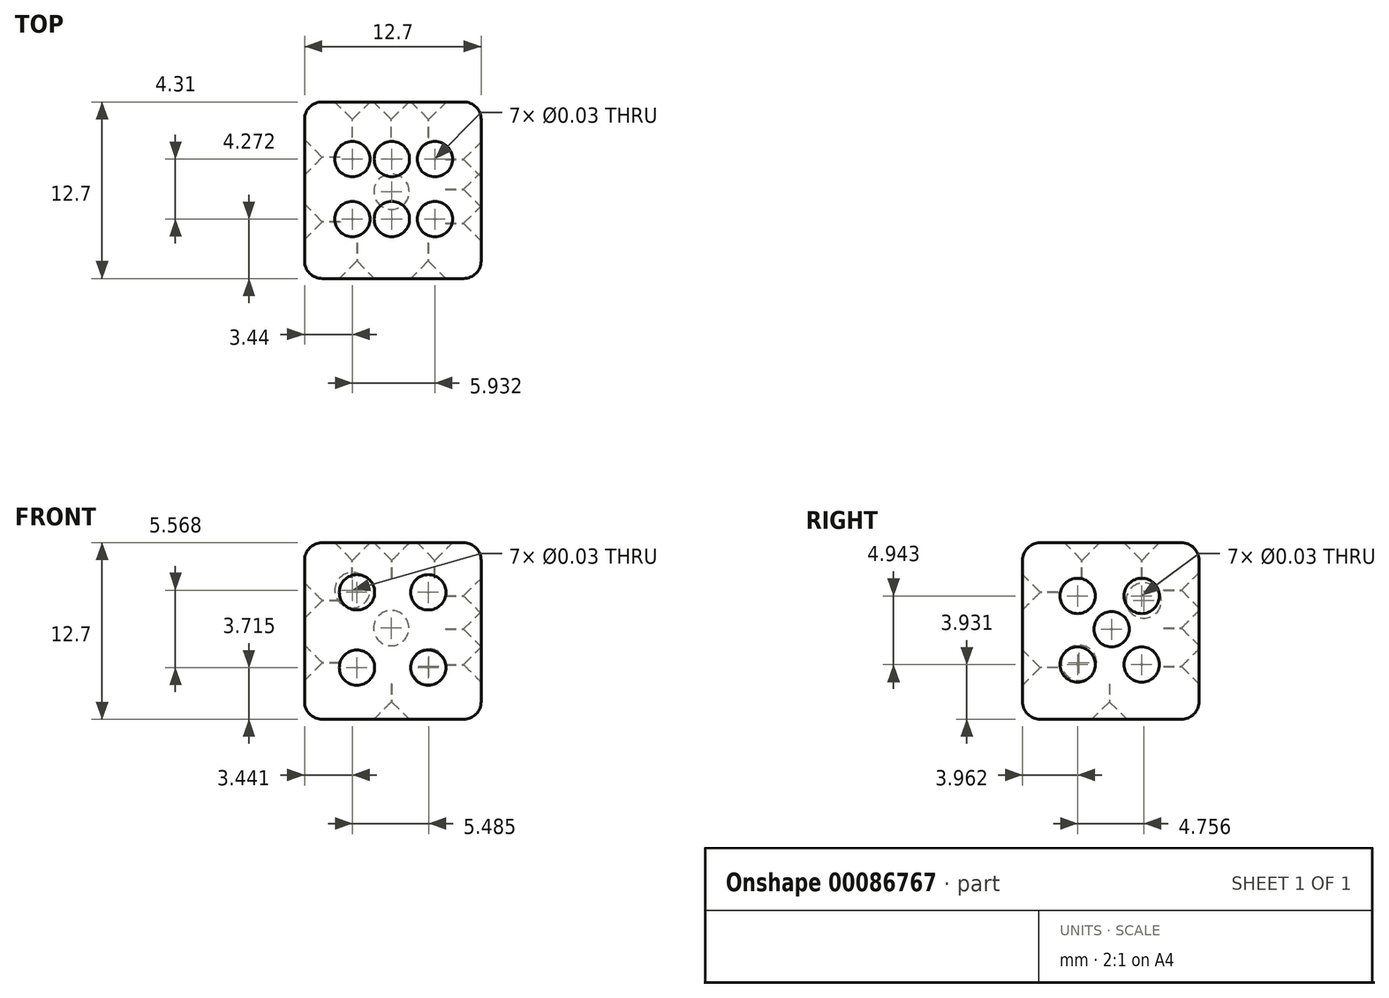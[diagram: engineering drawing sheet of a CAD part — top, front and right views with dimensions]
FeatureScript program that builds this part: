
annotation { "Feature Type Name" : "Feature", "Feature Type Description" : "" }
export const myFeature = defineFeature(function(context is Context, id is Id, definition is map)
    precondition{}
    {
        {
            var Q0;
            Q0=qCreatedBy(makeId("Front.planeOp"),FACE);
            var sketch = newSketch(context, id + "F0", { "sketchPlane" : qUnion([Q0])});
            skLineSegment(sketch, "E0.bottom", {"start": v(-48.45, 33.38) * mm, "end": v(-35.75, 33.38) * mm});
            skLineSegment(sketch, "E0.top", {"start": v(-48.45, 20.68) * mm, "end": v(-35.75, 20.68) * mm});
            skLineSegment(sketch, "E0.left", {"start": v(-48.45, 33.38) * mm, "end": v(-48.45, 20.68) * mm});
            skLineSegment(sketch, "E0.right", {"start": v(-35.75, 33.38) * mm, "end": v(-35.75, 20.68) * mm});
            skSolve(sketch);
        }
        {
            var Q0;
            Q0=makeQuery(id+"F0.imprint","IMPRINT",FACE,{"disambiguationData":[TD([[makeQuery(id+"F0.imprint","IMPRINT",EDGE,{"derivedFrom":sQuery(id+"F0.wireOp",EDGE,"E0.bottom")}),-1.0]])]});
            extrude(context, id + "F1", {"entities" : qUnion([Q0]), "depth" : 12.7 * mm});
        }
        {
            var Q0;
            Q0=makeQuery(id+"F1.opExtrude","SWEPT_EDGE",EDGE,{"disambiguationData":[OSD([sQuery(id+"F0.wireOp",EDGE,"E0.bottom"),sQuery(id+"F0.wireOp",EDGE,"E0.left")])]});
            var Q1;
            Q1=makeQuery(id+"F1.opExtrude","CAP_EDGE",EDGE,{"disambiguationData":[OSD([sQuery(id+"F0.wireOp",EDGE,"E0.bottom")])],"isStart":false});
            var Q2;
            Q2=makeQuery(id+"F1.opExtrude","SWEPT_EDGE",EDGE,{"disambiguationData":[OSD([sQuery(id+"F0.wireOp",EDGE,"E0.bottom"),sQuery(id+"F0.wireOp",EDGE,"E0.right")])]});
            var Q3;
            Q3=makeQuery(id+"F1.opExtrude","CAP_EDGE",EDGE,{"disambiguationData":[OSD([sQuery(id+"F0.wireOp",EDGE,"E0.right")])],"isStart":false});
            var Q4;
            Q4=makeQuery(id+"F1.opExtrude","CAP_EDGE",EDGE,{"disambiguationData":[OSD([sQuery(id+"F0.wireOp",EDGE,"E0.left")])],"isStart":false});
            var Q5;
            Q5=makeQuery(id+"F1.opExtrude","CAP_EDGE",EDGE,{"disambiguationData":[OSD([sQuery(id+"F0.wireOp",EDGE,"E0.bottom")])],"isStart":true});
            var Q6;
            Q6=makeQuery(id+"F1.opExtrude","CAP_EDGE",EDGE,{"disambiguationData":[OSD([sQuery(id+"F0.wireOp",EDGE,"E0.top")])],"isStart":false});
            var Q7;
            Q7=makeQuery(id+"F1.opExtrude","CAP_FACE",FACE,{"disambiguationData":[OSD([sQuery(id+"F0.wireOp",EDGE,"E0.bottom"),sQuery(id+"F0.wireOp",EDGE,"E0.top"),sQuery(id+"F0.wireOp",EDGE,"E0.left"),sQuery(id+"F0.wireOp",EDGE,"E0.right")])],"isStart":true});
            var Q8;
            Q8=makeQuery(id+"F1.opExtrude","SWEPT_FACE",FACE,{"disambiguationData":[OSD([sQuery(id+"F0.wireOp",EDGE,"E0.top")])]});
            fillet(context, id + "F2", {"entities" : qUnion([Q0, Q1, Q2, Q3, Q4, Q5, Q6, Q7, Q8]), "radius" : 1.27 * mm, "tangentPropagation" : true, "allowEdgeOverflow" : false});
        }
        {
            var Q0;
            Q0=makeQuery(id+"F1.opExtrude","SWEPT_FACE",FACE,{"disambiguationData":[OSD([sQuery(id+"F0.wireOp",EDGE,"E0.right")])]});
            var sketch = newSketch(context, id + "F3", { "sketchPlane" : qUnion([Q0])});
            skPoint(sketch, "E1", {"position": v(-8.74, 29.55) * mm});
            skPoint(sketch, "E2", {"position": v(-4.13, 29.55) * mm});
            skPoint(sketch, "E3", {"position": v(-4.13, 24.61) * mm});
            skPoint(sketch, "E4", {"position": v(-8.74, 24.61) * mm});
            skPoint(sketch, "E5", {"position": v(-6.3, 27.17) * mm});
            skSolve(sketch);
        }
        {
            var Q0;
            Q0=sQuery(id+"F3.wireOp",VERTEX,"E1");
            var Q1;
            Q1=sQuery(id+"F3.wireOp",VERTEX,"E2");
            var Q2;
            Q2=sQuery(id+"F3.wireOp",VERTEX,"E5");
            var Q3;
            Q3=sQuery(id+"F3.wireOp",VERTEX,"E3");
            var Q4;
            Q4=sQuery(id+"F3.wireOp",VERTEX,"E4");
            var Q5;
            Q5=makeQuery(id+"F1.opExtrude","SWEPT_BODY",BODY,{"disambiguationData":[OSD([sQuery(id+"F0.wireOp",EDGE,"E0.bottom"),sQuery(id+"F0.wireOp",EDGE,"E0.top"),sQuery(id+"F0.wireOp",EDGE,"E0.left"),sQuery(id+"F0.wireOp",EDGE,"E0.right")])]});
            hole(context, id + "F4", {"style" : HoleStyle.C_SINK, "endStyle" : HoleEndStyle.BLIND, "holeDiameter" : 0.03 * mm, "cSinkDiameter" : 2.54 * mm, "cSinkAngle" : 90 * degree, "holeDepth" : 2.54 * mm, "startFromSketch" : true, "locations" : qUnion([Q0, Q1, Q2, Q3, Q4]), "scope" : qUnion([Q5])});
        }
        {
            var Q0;
            Q0=makeQuery(id+"F1.opExtrude","CAP_FACE",FACE,{"disambiguationData":[OSD([sQuery(id+"F0.wireOp",EDGE,"E0.bottom"),sQuery(id+"F0.wireOp",EDGE,"E0.top"),sQuery(id+"F0.wireOp",EDGE,"E0.left"),sQuery(id+"F0.wireOp",EDGE,"E0.right")])],"isStart":false});
            var sketch = newSketch(context, id + "F5", { "sketchPlane" : qUnion([Q0])});
            skPoint(sketch, "E6", {"position": v(-44.68, 29.8) * mm});
            skPoint(sketch, "E7", {"position": v(-39.55, 29.8) * mm});
            skPoint(sketch, "E8", {"position": v(-39.55, 24.4) * mm});
            skPoint(sketch, "E9", {"position": v(-44.68, 24.4) * mm});
            skSolve(sketch);
        }
        {
            var Q0;
            Q0=sQuery(id+"F5.wireOp",VERTEX,"E6");
            var Q1;
            Q1=sQuery(id+"F5.wireOp",VERTEX,"E7");
            var Q2;
            Q2=sQuery(id+"F5.wireOp",VERTEX,"E8");
            var Q3;
            Q3=sQuery(id+"F5.wireOp",VERTEX,"E9");
            var Q4;
            Q4=makeQuery(id+"F1.opExtrude","SWEPT_BODY",BODY,{"disambiguationData":[OSD([sQuery(id+"F0.wireOp",EDGE,"E0.bottom"),sQuery(id+"F0.wireOp",EDGE,"E0.top"),sQuery(id+"F0.wireOp",EDGE,"E0.left"),sQuery(id+"F0.wireOp",EDGE,"E0.right")])]});
            hole(context, id + "F6", {"style" : HoleStyle.C_SINK, "endStyle" : HoleEndStyle.BLIND, "holeDiameter" : 0.03 * mm, "cSinkDiameter" : 2.54 * mm, "cSinkAngle" : 90 * degree, "holeDepth" : 2.54 * mm, "startFromSketch" : true, "locations" : qUnion([Q0, Q1, Q2, Q3]), "scope" : qUnion([Q4])});
        }
        {
            var Q0;
            Q0=makeQuery(id+"F1.opExtrude","SWEPT_FACE",FACE,{"disambiguationData":[OSD([sQuery(id+"F0.wireOp",EDGE,"E0.left")])]});
            var sketch = newSketch(context, id + "F7", { "sketchPlane" : qUnion([Q0])});
            skPoint(sketch, "E10", {"position": v(3.98, 29.22) * mm});
            skPoint(sketch, "E11", {"position": v(8.63, 24.74) * mm});
            skSolve(sketch);
        }
        {
            var Q0;
            Q0=sQuery(id+"F7.wireOp",VERTEX,"E10");
            var Q1;
            Q1=sQuery(id+"F7.wireOp",VERTEX,"E11");
            var Q2;
            Q2=makeQuery(id+"F1.opExtrude","SWEPT_BODY",BODY,{"disambiguationData":[OSD([sQuery(id+"F0.wireOp",EDGE,"E0.bottom"),sQuery(id+"F0.wireOp",EDGE,"E0.top"),sQuery(id+"F0.wireOp",EDGE,"E0.left"),sQuery(id+"F0.wireOp",EDGE,"E0.right")])]});
            hole(context, id + "F8", {"style" : HoleStyle.C_SINK, "endStyle" : HoleEndStyle.BLIND, "holeDiameter" : 0.03 * mm, "cSinkDiameter" : 2.54 * mm, "cSinkAngle" : 90 * degree, "holeDepth" : 2.54 * mm, "startFromSketch" : true, "locations" : qUnion([Q0, Q1]), "scope" : qUnion([Q2])});
        }
        {
            var Q0;
            Q0=makeQuery(id+"F1.opExtrude","CAP_FACE",FACE,{"disambiguationData":[OSD([sQuery(id+"F0.wireOp",EDGE,"E0.bottom"),sQuery(id+"F0.wireOp",EDGE,"E0.top"),sQuery(id+"F0.wireOp",EDGE,"E0.left"),sQuery(id+"F0.wireOp",EDGE,"E0.right")])],"isStart":true});
            var sketch = newSketch(context, id + "F9", { "sketchPlane" : qUnion([Q0])});
            skPoint(sketch, "E12", {"position": v(45, 29.96) * mm});
            skPoint(sketch, "E13", {"position": v(42.21, 27.24) * mm});
            skPoint(sketch, "E14", {"position": v(39.52, 24.48) * mm});
            skSolve(sketch);
        }
        {
            var Q0;
            Q0=sQuery(id+"F9.wireOp",VERTEX,"E12");
            var Q1;
            Q1=sQuery(id+"F9.wireOp",VERTEX,"E13");
            var Q2;
            Q2=sQuery(id+"F9.wireOp",VERTEX,"E14");
            var Q3;
            Q3=makeQuery(id+"F1.opExtrude","SWEPT_BODY",BODY,{"disambiguationData":[OSD([sQuery(id+"F0.wireOp",EDGE,"E0.bottom"),sQuery(id+"F0.wireOp",EDGE,"E0.top"),sQuery(id+"F0.wireOp",EDGE,"E0.left"),sQuery(id+"F0.wireOp",EDGE,"E0.right")])]});
            hole(context, id + "F10", {"style" : HoleStyle.C_SINK, "endStyle" : HoleEndStyle.BLIND, "holeDiameter" : 0.03 * mm, "cSinkDiameter" : 2.54 * mm, "cSinkAngle" : 90 * degree, "holeDepth" : 2.54 * mm, "startFromSketch" : true, "locations" : qUnion([Q0, Q1, Q2]), "scope" : qUnion([Q3])});
        }
        {
            var Q0;
            Q0=makeQuery(id+"F1.opExtrude","SWEPT_FACE",FACE,{"disambiguationData":[OSD([sQuery(id+"F0.wireOp",EDGE,"E0.bottom")])]});
            var sketch = newSketch(context, id + "F11", { "sketchPlane" : qUnion([Q0])});
            skPoint(sketch, "E15", {"position": v(-39.08, -4.12) * mm});
            skPoint(sketch, "E16", {"position": v(-42.17, -4.12) * mm});
            skPoint(sketch, "E17", {"position": v(-45.01, -4.12) * mm});
            skPoint(sketch, "E18", {"position": v(-39.08, -8.43) * mm});
            skPoint(sketch, "E19", {"position": v(-42.17, -8.43) * mm});
            skPoint(sketch, "E20", {"position": v(-45.01, -8.43) * mm});
            skSolve(sketch);
        }
        {
            var Q0;
            Q0=sQuery(id+"F11.wireOp",VERTEX,"E15");
            var Q1;
            Q1=sQuery(id+"F11.wireOp",VERTEX,"E16");
            var Q2;
            Q2=sQuery(id+"F11.wireOp",VERTEX,"E17");
            var Q3;
            Q3=sQuery(id+"F11.wireOp",VERTEX,"E20");
            var Q4;
            Q4=sQuery(id+"F11.wireOp",VERTEX,"E19");
            var Q5;
            Q5=sQuery(id+"F11.wireOp",VERTEX,"E18");
            var Q6;
            Q6=makeQuery(id+"F1.opExtrude","SWEPT_BODY",BODY,{"disambiguationData":[OSD([sQuery(id+"F0.wireOp",EDGE,"E0.bottom"),sQuery(id+"F0.wireOp",EDGE,"E0.top"),sQuery(id+"F0.wireOp",EDGE,"E0.left"),sQuery(id+"F0.wireOp",EDGE,"E0.right")])]});
            hole(context, id + "F12", {"style" : HoleStyle.C_SINK, "endStyle" : HoleEndStyle.BLIND, "holeDiameter" : 0.03 * mm, "cSinkDiameter" : 2.54 * mm, "cSinkAngle" : 90 * degree, "holeDepth" : 2.54 * mm, "startFromSketch" : true, "locations" : qUnion([Q0, Q1, Q2, Q3, Q4, Q5]), "scope" : qUnion([Q6])});
        }
        {
            var Q0;
            Q0=makeQuery(id+"F1.opExtrude","SWEPT_FACE",FACE,{"disambiguationData":[OSD([sQuery(id+"F0.wireOp",EDGE,"E0.top")])]});
            var sketch = newSketch(context, id + "F13", { "sketchPlane" : qUnion([Q0])});
            skPoint(sketch, "E21", {"position": v(-42.2, 6.45) * mm});
            skSolve(sketch);
        }
        {
            var Q0;
            Q0=sQuery(id+"F13.wireOp",VERTEX,"E21");
            var Q1;
            Q1=makeQuery(id+"F1.opExtrude","SWEPT_BODY",BODY,{"disambiguationData":[OSD([sQuery(id+"F0.wireOp",EDGE,"E0.bottom"),sQuery(id+"F0.wireOp",EDGE,"E0.top"),sQuery(id+"F0.wireOp",EDGE,"E0.left"),sQuery(id+"F0.wireOp",EDGE,"E0.right")])]});
            hole(context, id + "F14", {"style" : HoleStyle.C_SINK, "endStyle" : HoleEndStyle.BLIND, "holeDiameter" : 0.03 * mm, "cSinkDiameter" : 2.54 * mm, "cSinkAngle" : 90 * degree, "holeDepth" : 2.54 * mm, "startFromSketch" : true, "locations" : qUnion([Q0]), "scope" : qUnion([Q1])});
        }
    });
